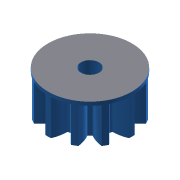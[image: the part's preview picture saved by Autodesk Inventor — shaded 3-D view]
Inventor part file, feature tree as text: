
AUTODESK INVENTOR PART (.ipt)
format: ipt  version: 2016 (Build 200138000, 138)  size: 250,368 bytes
history: native  units: mm (DEFAULTED — no unit token found)
features: sketch x7, extrude x4, plane x4, other x3, loft x1
ambient origin geometry x8: Origin, YZ Plane, XZ Plane, XY Plane, X Axis, Y Axis, Z Axis, Center Point
bodies: Solid1 (feature_tree)
feature tree (19):
  extrude  "Extrusion1"  Depth=10.0mm TaperAngle=0.0deg
  plane  "Work Plane2"
  plane  "Work Plane8"
  plane  "Work Plane9"
  other  "Spur Gear"
  extrude  "Extrusion3"  Depth=10.0mm TaperAngle=0.0deg
  sketch  "Sketch5"  dims[d39=0.0mm d41=0.0mm]
  plane  "Work Plane11"
  loft  "Loft1"
  extrude  "Extrusion4"  TaperAngle=0.0deg  [1 undecoded]
  extrude  "Extrusion5"  Depth=30.0mm
  sketch  "Sketch1"  dims[d0=23.646106mm d1=10.0mm d2=0.0mm]
  sketch  "Sketch2"  dims[d3=20.0mm d4=10.0mm d5=0.0mm]
  other  "Srf1"
  sketch  "Sketch4"  dims[d16=30.0mm d17=0.0mm d34=15.0deg]
  sketch  "Sketch6"  dims[d43=30.0mm d46=30.0mm]
  sketch  "Sketch7"  dims[d47=0.0mm d48=0.0mm]
  sketch  "Sketch8"  dims[d52=5.1mm d53=10.0mm d54=0.0mm d55=-1.0mm d56=0.0mm d57=90.0deg d58=0.0mm d59=90.0deg d60=1.0mm d61=0.0mm d62=20.0mm d63=0.0mm]
  other  "Pitch Diameter"
note: 1 required parameter value undecoded (feature->parameter linkage not recoverable at this tier; creation-order binding heuristic only, values carry confidence <= 0.55)
